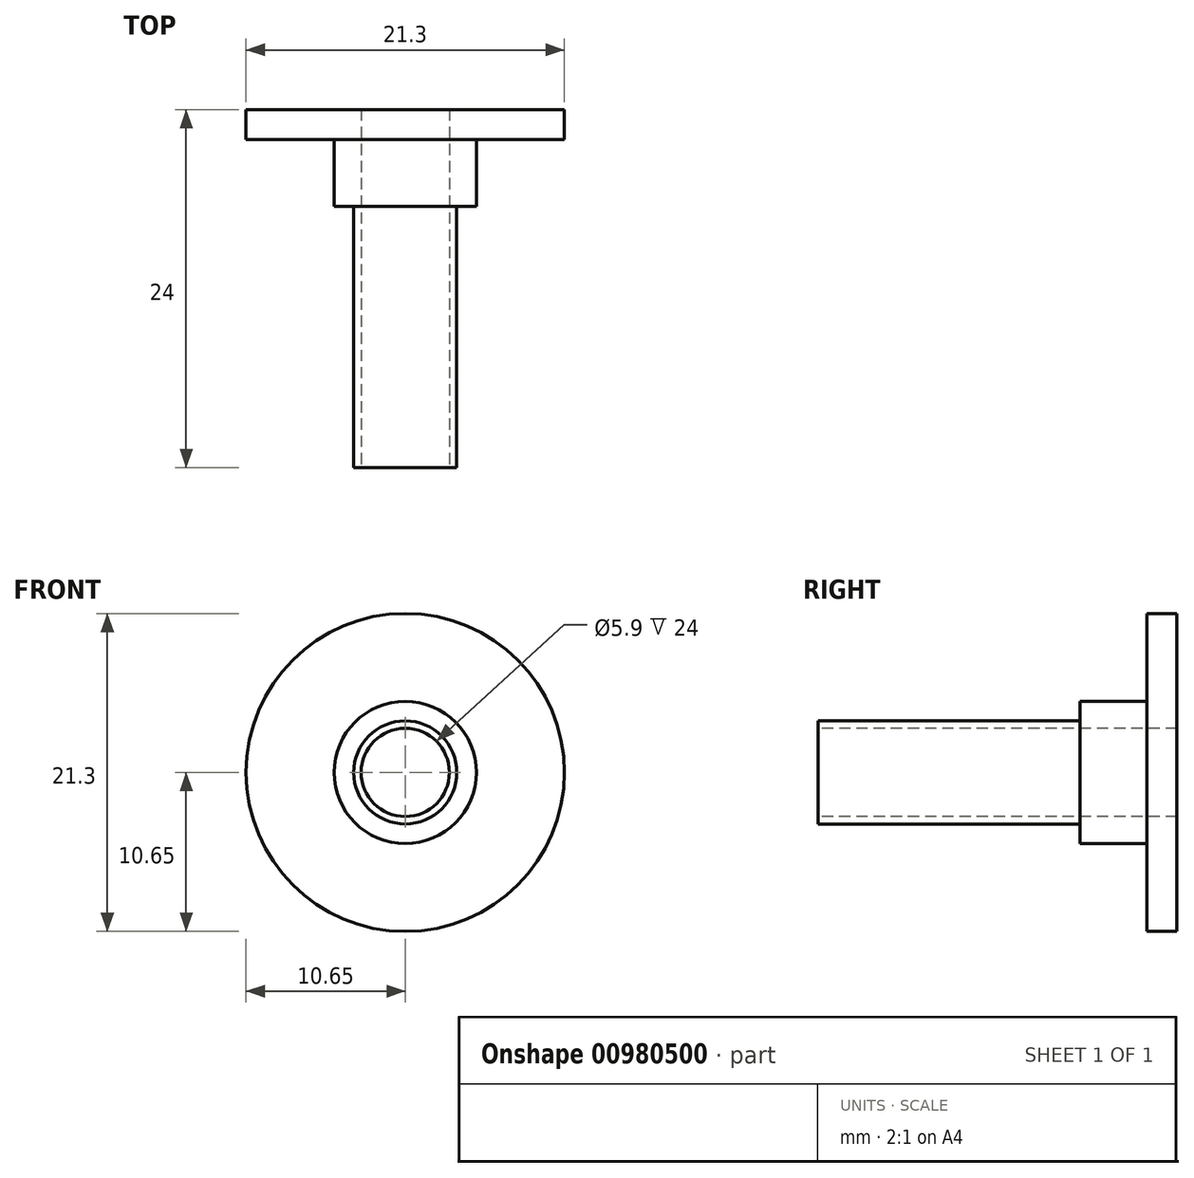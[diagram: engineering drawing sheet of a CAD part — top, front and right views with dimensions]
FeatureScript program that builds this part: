
annotation { "Feature Type Name" : "Feature", "Feature Type Description" : "" }
export const myFeature = defineFeature(function(context is Context, id is Id, definition is map)
    precondition{}
    {
        {
            var Q0;
            Q0=qCreatedBy(makeId("Front.planeOp"),FACE);
            var sketch = newSketch(context, id + "F0", { "sketchPlane" : qUnion([Q0])});
            skCircle(sketch, "E0", {"center": v(0, 0) * mm, "radius": 3.45 * mm});
            skSolve(sketch);
        }
        {
            var Q0;
            Q0=makeQuery(id+"F0.imprint","IMPRINT",FACE,{"disambiguationData":[TD([[makeQuery(id+"F0.imprint","IMPRINT",EDGE,{"derivedFrom":sQuery(id+"F0.wireOp",EDGE,"E0")}),1.0]])]});
            extrude(context, id + "F1", {"entities" : qUnion([Q0]), "depth" : 17.5 * mm, "offsetDistance" : 25 * mm});
        }
        {
            var Q0;
            Q0=makeQuery(id+"F1.opExtrude","CAP_FACE",FACE,{"disambiguationData":[OSD([sQuery(id+"F0.wireOp",EDGE,"E0")])],"isStart":true});
            var sketch = newSketch(context, id + "F2", { "sketchPlane" : qUnion([Q0])});
            skCircle(sketch, "E1", {"center": v(0, 0) * mm, "radius": 4.76 * mm});
            skSolve(sketch);
        }
        {
            var Q0;
            Q0=makeQuery(id+"F1.opExtrude","CAP_FACE",FACE,{"disambiguationData":[OSD([sQuery(id+"F0.wireOp",EDGE,"E0")])],"isStart":true});
            extrude(context, id + "F3", {"entities" : qUnion([Q0]), "operationType" : NewBodyOperationType.ADD, "depth" : 4.5 * mm, "offsetDistance" : 25 * mm});
        }
        {
            var Q0;
            Q0=makeQuery(id+"F2.imprint","IMPRINT",FACE,{"disambiguationData":[TD([[makeQuery(id+"F2.imprint","IMPRINT",EDGE,{"derivedFrom":sQuery(id+"F2.wireOp",EDGE,"E1")}),1.0]])]});
            extrude(context, id + "F4", {"entities" : qUnion([Q0]), "operationType" : NewBodyOperationType.ADD, "depth" : 4.5 * mm, "offsetDistance" : 25 * mm});
        }
        {
            var Q0;
            {var subQ0=sQuery(id+"F0.wireOp",EDGE,"E0");Q0=makeQuery(id+"F4.boolean.opBoolean","MERGE",FACE,{"derivedFrom":[makeQuery(id+"F3.opExtrude","CAP_FACE",FACE,{"disambiguationData":[OSD([subQ0])],"isStart":false}),makeQuery(id+"F4.opExtrude","CAP_FACE",FACE,{"disambiguationData":[OSD([subQ0,sQuery(id+"F2.wireOp",EDGE,"E1")])],"isStart":false})]});}
            var sketch = newSketch(context, id + "F5", { "sketchPlane" : qUnion([Q0])});
            skCircle(sketch, "E2", {"center": v(0, 0) * mm, "radius": 10.65 * mm});
            skSolve(sketch);
        }
        {
            var Q0;
            Q0=makeQuery(id+"F5.imprint","IMPRINT",FACE,{"disambiguationData":[TD([[makeQuery(id+"F5.imprint","IMPRINT",EDGE,{"derivedFrom":sQuery(id+"F5.wireOp",EDGE,"E2")}),1.0]])]});
            var Q1;
            Q1=makeQuery(id+"F5.imprint","IMPRINT",FACE,{"disambiguationData":[TD([[makeQuery(id+"F5.imprint","IMPRINT",EDGE,{"derivedFrom":makeQuery(id+"F4.opExtrude","CAP_EDGE",EDGE,{"disambiguationData":[OSD([sQuery(id+"F2.wireOp",EDGE,"E1")])],"isStart":false})}),1.0]])]});
            extrude(context, id + "F6", {"entities" : qUnion([Q0, Q1]), "operationType" : NewBodyOperationType.ADD, "depth" : 2 * mm, "offsetDistance" : 25 * mm});
        }
        {
            var Q0;
            Q0=makeQuery(id+"F1.opExtrude","CAP_FACE",FACE,{"disambiguationData":[OSD([sQuery(id+"F0.wireOp",EDGE,"E0")])],"isStart":false});
            var sketch = newSketch(context, id + "F7", { "sketchPlane" : qUnion([Q0])});
            skCircle(sketch, "E3", {"center": v(0, 0) * mm, "radius": 2.95 * mm});
            skSolve(sketch);
        }
        {
            var Q0;
            Q0 = qSketchRegion(id + "F7", true);
            extrude(context, id + "F8", {"entities" : qUnion([Q0]), "operationType" : NewBodyOperationType.REMOVE, "oppositeDirection" : true, "depth" : 28 * mm, "offsetDistance" : 25 * mm});
        }
    });
